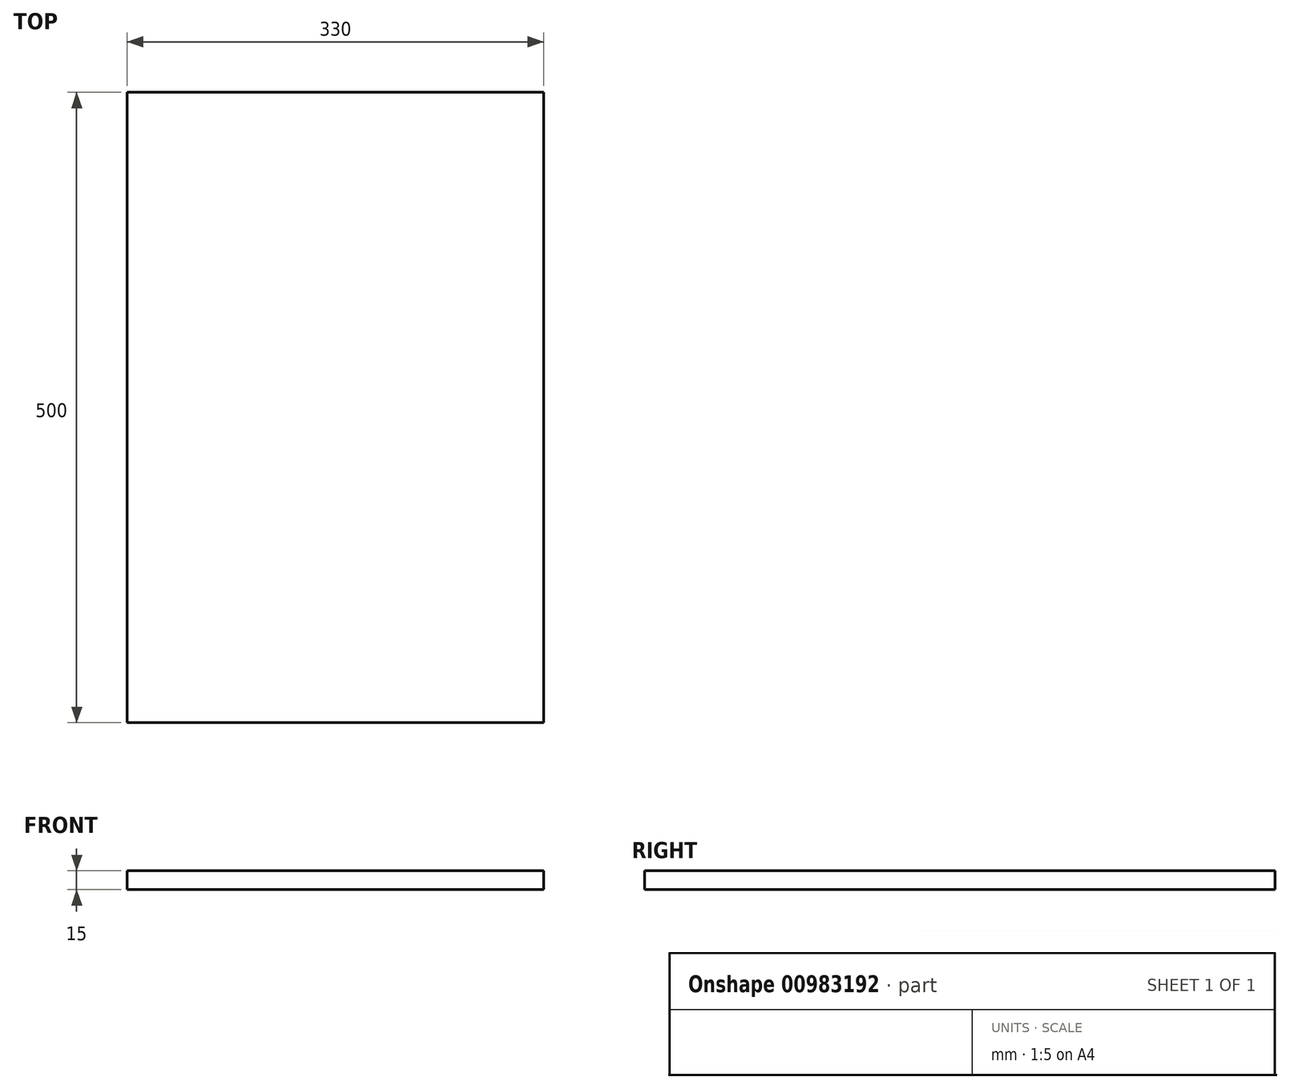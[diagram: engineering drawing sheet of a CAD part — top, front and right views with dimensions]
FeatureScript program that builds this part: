
annotation { "Feature Type Name" : "Feature", "Feature Type Description" : "" }
export const myFeature = defineFeature(function(context is Context, id is Id, definition is map)
    precondition{}
    {
        {
            var Q0;
            Q0=qCreatedBy(makeId("Top.planeOp"),FACE);
            var sketch = newSketch(context, id + "F0", { "sketchPlane" : qUnion([Q0])});
            skLineSegment(sketch, "E0.bottom", {"start": v(165, 250) * mm, "end": v(-165, 250) * mm});
            skLineSegment(sketch, "E0.top", {"start": v(165, -250) * mm, "end": v(-165, -250) * mm});
            skLineSegment(sketch, "E0.left", {"start": v(165, 250) * mm, "end": v(165, -250) * mm});
            skLineSegment(sketch, "E0.right", {"start": v(-165, 250) * mm, "end": v(-165, -250) * mm});
            skPoint(sketch, "E0.middle", {"position": v(0, 0) * mm});
            skSolve(sketch);
        }
        {
            var Q0;
            Q0 = qSketchRegion(id + "F0", true);
            extrude(context, id + "F1", {"entities" : qUnion([Q0]), "depth" : 15 * mm, "offsetDistance" : 25 * mm});
        }
    });
